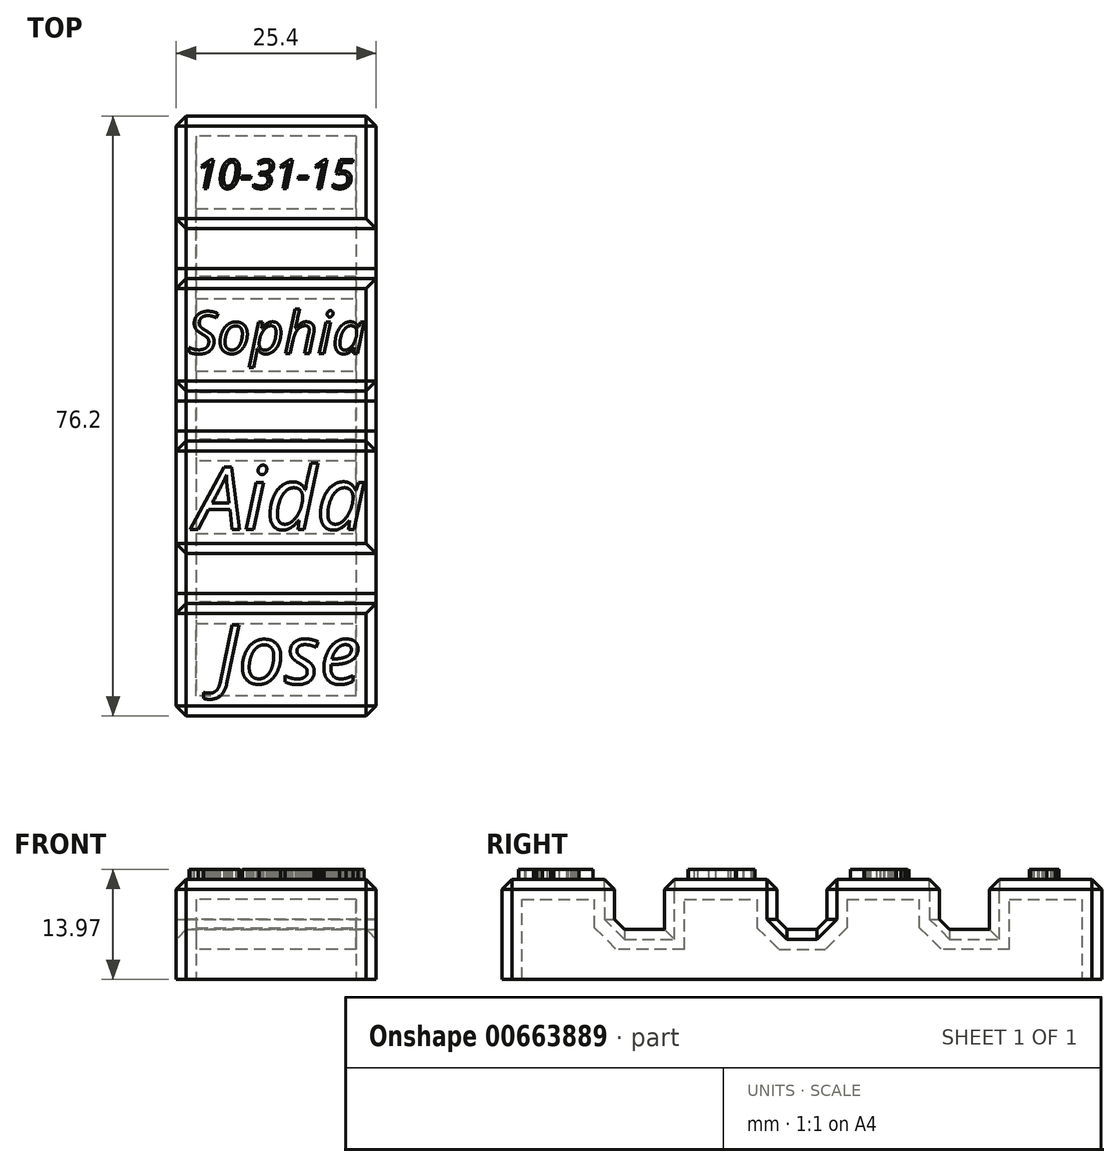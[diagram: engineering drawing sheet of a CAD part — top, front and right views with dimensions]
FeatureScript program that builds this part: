
annotation { "Feature Type Name" : "Feature", "Feature Type Description" : "" }
export const myFeature = defineFeature(function(context is Context, id is Id, definition is map)
    precondition{}
    {
        {
            var Q0;
            Q0=qCreatedBy(makeId("Top.planeOp"),FACE);
            var sketch = newSketch(context, id + "F0", { "sketchPlane" : qUnion([Q0])});
            skLineSegment(sketch, "E0.bottom", {"start": v(12.7, 38.1) * mm, "end": v(-12.7, 38.1) * mm});
            skLineSegment(sketch, "E0.top", {"start": v(12.7, -38.1) * mm, "end": v(-12.7, -38.1) * mm});
            skLineSegment(sketch, "E0.left", {"start": v(12.7, 38.1) * mm, "end": v(12.7, -38.1) * mm});
            skLineSegment(sketch, "E0.right", {"start": v(-12.7, 38.1) * mm, "end": v(-12.7, -38.1) * mm});
            skPoint(sketch, "E0.middle", {"position": v(0, 0) * mm});
            skSolve(sketch);
        }
        {
            var Q0;
            Q0 = qSketchRegion(id + "F0", true);
            extrude(context, id + "F1", {"entities" : qUnion([Q0]), "depth" : 12.7 * mm, "offsetDistance" : 25.4 * mm});
        }
        {
            var Q0;
            Q0=makeQuery(id+"F1.opExtrude","SWEPT_FACE",FACE,{"disambiguationData":[OSD([sQuery(id+"F0.wireOp",EDGE,"E0.left")])]});
            var sketch = newSketch(context, id + "F2", { "sketchPlane" : qUnion([Q0])});
            skLineSegment(sketch, "E1", {"start": v(-38.1, 6.35) * mm, "end": v(38.1, 6.35) * mm, "construction": true});
            skLineSegment(sketch, "E2.bottom", {"start": v(3.17, 6.35) * mm, "end": v(-3.18, 6.35) * mm});
            skLineSegment(sketch, "E2.top", {"start": v(3.17, 19.05) * mm, "end": v(-3.18, 19.05) * mm});
            skLineSegment(sketch, "E2.left", {"start": v(3.17, 6.35) * mm, "end": v(3.17, 19.05) * mm});
            skLineSegment(sketch, "E2.right", {"start": v(-3.18, 6.35) * mm, "end": v(-3.18, 19.05) * mm});
            skPoint(sketch, "E2.middle", {"position": v(0, 12.7) * mm});
            skLineSegment(sketch, "E3.bottom", {"start": v(23.83, 6.35) * mm, "end": v(17.48, 6.35) * mm});
            skLineSegment(sketch, "E3.top", {"start": v(23.83, 19.05) * mm, "end": v(17.48, 19.05) * mm});
            skLineSegment(sketch, "E3.left", {"start": v(23.83, 6.35) * mm, "end": v(23.83, 19.05) * mm});
            skLineSegment(sketch, "E3.right", {"start": v(17.48, 6.35) * mm, "end": v(17.48, 19.05) * mm});
            skPoint(sketch, "E3.middle", {"position": v(20.65, 12.7) * mm});
            skLineSegment(sketch, "E4.bottom", {"start": v(-17.48, 6.35) * mm, "end": v(-23.83, 6.35) * mm});
            skLineSegment(sketch, "E4.top", {"start": v(-17.48, 19.05) * mm, "end": v(-23.83, 19.05) * mm});
            skLineSegment(sketch, "E4.left", {"start": v(-17.48, 6.35) * mm, "end": v(-17.48, 19.05) * mm});
            skLineSegment(sketch, "E4.right", {"start": v(-23.83, 6.35) * mm, "end": v(-23.83, 19.05) * mm});
            skPoint(sketch, "E4.middle", {"position": v(-20.65, 12.7) * mm});
            skSolve(sketch);
        }
        {
            var Q0;
            Q0 = qSketchRegion(id + "F2", true);
            extrude(context, id + "F3", {"entities" : qUnion([Q0]), "operationType" : NewBodyOperationType.REMOVE, "endBound" : BoundingType.THROUGH_ALL, "oppositeDirection" : true, "depth" : 25.4 * mm, "offsetDistance" : 25.4 * mm});
        }
        {
            var Q0;
            {var subQ0=sQuery(id+"F0.wireOp",EDGE,"E0.bottom");var subQ1=sQuery(id+"F0.wireOp",EDGE,"E0.right");var subQ2=sQuery(id+"F0.wireOp",EDGE,"E0.left");Q0=makeQuery(id+"F3.boolean.opBoolean","SPLIT",FACE,{"disambiguationData":[TD([makeQuery(id+"F1.opExtrude","SWEPT_FACE",FACE,{"disambiguationData":[OSD([subQ0])]})])],"derivedFrom":makeQuery(id+"F1.opExtrude","CAP_FACE",FACE,{"disambiguationData":[OSD([subQ0,sQuery(id+"F0.wireOp",EDGE,"E0.top"),subQ2,subQ1])],"isStart":false})});}
            var Q1;
            Q1=makeQuery(id+"F3.boolean.opBoolean","COPY",EDGE,{"derivedFrom":makeQuery(id+"F3.opExtrude","CAP_EDGE",EDGE,{"disambiguationData":[OSD([sQuery(id+"F2.wireOp",EDGE,"E4.bottom")])],"isStart":true})});
            var Q2;
            Q2=makeQuery(id+"F3.boolean.opBoolean","COPY",FACE,{"derivedFrom":makeQuery(id+"F3.opExtrude","SWEPT_FACE",FACE,{"disambiguationData":[OSD([sQuery(id+"F2.wireOp",EDGE,"E2.bottom")])]})});
            var Q3;
            Q3=makeQuery(id+"F3.boolean.opBoolean","COPY",EDGE,{"derivedFrom":makeQuery(id+"F3.opExtrude","CAP_EDGE",EDGE,{"disambiguationData":[OSD([sQuery(id+"F2.wireOp",EDGE,"E3.right")])],"isStart":true})});
            var Q4;
            Q4=makeQuery(id+"F3.boolean.opBoolean","COPY",EDGE,{"derivedFrom":makeQuery(id+"F3.opExtrude","CAP_EDGE",EDGE,{"disambiguationData":[OSD([sQuery(id+"F2.wireOp",EDGE,"E3.left")])],"isStart":true})});
            var Q5;
            Q5=makeQuery(id+"F3.boolean.opBoolean","COPY",EDGE,{"derivedFrom":makeQuery(id+"F3.opExtrude","CAP_EDGE",EDGE,{"disambiguationData":[OSD([sQuery(id+"F2.wireOp",EDGE,"E4.right")])],"isStart":true})});
            var Q6;
            Q6=makeQuery(id+"F3.boolean.opBoolean","COPY",EDGE,{"derivedFrom":makeQuery(id+"F3.opExtrude","CAP_EDGE",EDGE,{"disambiguationData":[OSD([sQuery(id+"F2.wireOp",EDGE,"E4.left")])],"isStart":true})});
            var Q7;
            {var subQ0=sQuery(id+"F0.wireOp",EDGE,"E0.top");var subQ1=sQuery(id+"F0.wireOp",EDGE,"E0.left");var subQ2=sQuery(id+"F0.wireOp",EDGE,"E0.right");Q7=makeQuery(id+"F3.boolean.opBoolean","SPLIT",FACE,{"disambiguationData":[TD([makeQuery(id+"F1.opExtrude","SWEPT_FACE",FACE,{"disambiguationData":[OSD([subQ0])]})])],"derivedFrom":makeQuery(id+"F1.opExtrude","CAP_FACE",FACE,{"disambiguationData":[OSD([sQuery(id+"F0.wireOp",EDGE,"E0.bottom"),subQ0,subQ1,subQ2])],"isStart":false})});}
            var Q8;
            Q8=makeQuery(id+"F3.boolean.opBoolean","COPY",EDGE,{"derivedFrom":makeQuery(id+"F3.opExtrude","SWEPT_EDGE",EDGE,{"disambiguationData":[OSD([sQuery(id+"F2.wireOp",EDGE,"E4.bottom"),sQuery(id+"F2.wireOp",EDGE,"E4.right")])]})});
            var Q9;
            {var subQ0=sQuery(id+"F0.wireOp",EDGE,"E0.left");var subQ1=sQuery(id+"F0.wireOp",EDGE,"E0.right");Q9=makeQuery(id+"F3.boolean.opBoolean","SPLIT",FACE,{"disambiguationData":[TD([makeQuery(id+"F3.opExtrude","SWEPT_FACE",FACE,{"disambiguationData":[OSD([sQuery(id+"F2.wireOp",EDGE,"E2.right")])]})])],"derivedFrom":makeQuery(id+"F1.opExtrude","CAP_FACE",FACE,{"disambiguationData":[OSD([sQuery(id+"F0.wireOp",EDGE,"E0.bottom"),sQuery(id+"F0.wireOp",EDGE,"E0.top"),subQ0,subQ1])],"isStart":false})});}
            var Q10;
            {var subQ0=sQuery(id+"F0.wireOp",EDGE,"E0.left");var subQ1=sQuery(id+"F0.wireOp",EDGE,"E0.right");Q10=makeQuery(id+"F3.boolean.opBoolean","SPLIT",FACE,{"disambiguationData":[TD([makeQuery(id+"F3.opExtrude","SWEPT_FACE",FACE,{"disambiguationData":[OSD([sQuery(id+"F2.wireOp",EDGE,"E2.left")])]})])],"derivedFrom":makeQuery(id+"F1.opExtrude","CAP_FACE",FACE,{"disambiguationData":[OSD([sQuery(id+"F0.wireOp",EDGE,"E0.bottom"),sQuery(id+"F0.wireOp",EDGE,"E0.top"),subQ0,subQ1])],"isStart":false})});}
            var Q11;
            Q11=makeQuery(id+"F3.boolean.opBoolean","COPY",EDGE,{"derivedFrom":makeQuery(id+"F3.opExtrude","SWEPT_EDGE",EDGE,{"disambiguationData":[OSD([sQuery(id+"F2.wireOp",EDGE,"E3.bottom"),sQuery(id+"F2.wireOp",EDGE,"E3.right")])]})});
            var Q12;
            Q12=makeQuery(id+"F3.boolean.opBoolean","INTERSECT",EDGE,{"derivedFrom":[makeQuery(id+"F1.opExtrude","SWEPT_FACE",FACE,{"disambiguationData":[OSD([sQuery(id+"F0.wireOp",EDGE,"E0.right")])]}),makeQuery(id+"F3.opExtrude","SWEPT_FACE",FACE,{"disambiguationData":[OSD([sQuery(id+"F2.wireOp",EDGE,"E3.bottom")])]})]});
            var Q13;
            Q13=makeQuery(id+"F3.boolean.opBoolean","INTERSECT",EDGE,{"derivedFrom":[makeQuery(id+"F1.opExtrude","SWEPT_FACE",FACE,{"disambiguationData":[OSD([sQuery(id+"F0.wireOp",EDGE,"E0.right")])]}),makeQuery(id+"F3.opExtrude","SWEPT_FACE",FACE,{"disambiguationData":[OSD([sQuery(id+"F2.wireOp",EDGE,"E3.left")])]})]});
            var Q14;
            Q14=makeQuery(id+"F3.boolean.opBoolean","INTERSECT",EDGE,{"derivedFrom":[makeQuery(id+"F1.opExtrude","SWEPT_FACE",FACE,{"disambiguationData":[OSD([sQuery(id+"F0.wireOp",EDGE,"E0.right")])]}),makeQuery(id+"F3.opExtrude","SWEPT_FACE",FACE,{"disambiguationData":[OSD([sQuery(id+"F2.wireOp",EDGE,"E4.right")])]})]});
            var Q15;
            Q15=makeQuery(id+"F3.boolean.opBoolean","INTERSECT",EDGE,{"derivedFrom":[makeQuery(id+"F1.opExtrude","SWEPT_FACE",FACE,{"disambiguationData":[OSD([sQuery(id+"F0.wireOp",EDGE,"E0.right")])]}),makeQuery(id+"F3.opExtrude","SWEPT_FACE",FACE,{"disambiguationData":[OSD([sQuery(id+"F2.wireOp",EDGE,"E4.left")])]})]});
            var Q16;
            Q16=makeQuery(id+"F1.opExtrude","SWEPT_EDGE",EDGE,{"disambiguationData":[OSD([sQuery(id+"F0.wireOp",EDGE,"E0.bottom"),sQuery(id+"F0.wireOp",EDGE,"E0.right")])]});
            var Q17;
            Q17=makeQuery(id+"F1.opExtrude","SWEPT_EDGE",EDGE,{"disambiguationData":[OSD([sQuery(id+"F0.wireOp",EDGE,"E0.top"),sQuery(id+"F0.wireOp",EDGE,"E0.right")])]});
            var Q18;
            Q18=makeQuery(id+"F1.opExtrude","SWEPT_EDGE",EDGE,{"disambiguationData":[OSD([sQuery(id+"F0.wireOp",EDGE,"E0.top"),sQuery(id+"F0.wireOp",EDGE,"E0.left")])]});
            var Q19;
            Q19=makeQuery(id+"F1.opExtrude","SWEPT_EDGE",EDGE,{"disambiguationData":[OSD([sQuery(id+"F0.wireOp",EDGE,"E0.bottom"),sQuery(id+"F0.wireOp",EDGE,"E0.left")])]});
            var Q20;
            Q20=makeQuery(id+"F3.boolean.opBoolean","INTERSECT",EDGE,{"derivedFrom":[makeQuery(id+"F1.opExtrude","SWEPT_FACE",FACE,{"disambiguationData":[OSD([sQuery(id+"F0.wireOp",EDGE,"E0.right")])]}),makeQuery(id+"F3.opExtrude","SWEPT_FACE",FACE,{"disambiguationData":[OSD([sQuery(id+"F2.wireOp",EDGE,"E4.bottom")])]})]});
            chamfer(context, id + "F4", {"entities" : qUnion([Q0, Q1, Q2, Q3, Q4, Q5, Q6, Q7, Q8, Q9, Q10, Q11, Q12, Q13, Q14, Q15, Q16, Q17, Q18, Q19, Q20]), "width" : 1.27 * mm, "tangentPropagation" : true});
        }
        {
            var Q0;
            Q0=makeQuery(id+"F1.opExtrude","CAP_FACE",FACE,{"disambiguationData":[OSD([sQuery(id+"F0.wireOp",EDGE,"E0.bottom"),sQuery(id+"F0.wireOp",EDGE,"E0.top"),sQuery(id+"F0.wireOp",EDGE,"E0.left"),sQuery(id+"F0.wireOp",EDGE,"E0.right")])],"isStart":true});
            shell(context, id + "F5", {"entities" : qUnion([Q0]), "thickness" : 2.54 * mm});
        }
        {
            var Q0;
            {var subQ0=sQuery(id+"F0.wireOp",EDGE,"E0.top");var subQ1=sQuery(id+"F0.wireOp",EDGE,"E0.left");var subQ2=sQuery(id+"F0.wireOp",EDGE,"E0.right");Q0=makeQuery(id+"F3.boolean.opBoolean","SPLIT",FACE,{"disambiguationData":[TD([makeQuery(id+"F1.opExtrude","SWEPT_FACE",FACE,{"disambiguationData":[OSD([subQ0])]})])],"derivedFrom":makeQuery(id+"F1.opExtrude","CAP_FACE",FACE,{"disambiguationData":[OSD([sQuery(id+"F0.wireOp",EDGE,"E0.bottom"),subQ0,subQ1,subQ2])],"isStart":false})});}
            var sketch = newSketch(context, id + "F6", { "sketchPlane" : qUnion([Q0])});
            skText(sketch, "E5", { "text": "Jose", "fontName": "OpenSans-Italic.ttf"});
            const initialGuessF6  = {"E5": [-0.0076, -0.03402, 1, 0, 0.00754]};
            skSetInitialGuess(sketch, initialGuessF6);
            skSolve(sketch);
        }
        {
            var Q0;
            Q0 = qSketchRegion(id + "F6", true);
            extrude(context, id + "F7", {"entities" : qUnion([Q0]), "operationType" : NewBodyOperationType.ADD, "depth" : 1.27 * mm, "offsetDistance" : 25.4 * mm});
        }
        {
            var Q0;
            {var subQ0=sQuery(id+"F0.wireOp",EDGE,"E0.left");var subQ1=sQuery(id+"F0.wireOp",EDGE,"E0.right");Q0=makeQuery(id+"F3.boolean.opBoolean","SPLIT",FACE,{"disambiguationData":[TD([makeQuery(id+"F3.opExtrude","SWEPT_FACE",FACE,{"disambiguationData":[OSD([sQuery(id+"F2.wireOp",EDGE,"E2.right")])]})])],"derivedFrom":makeQuery(id+"F1.opExtrude","CAP_FACE",FACE,{"disambiguationData":[OSD([sQuery(id+"F0.wireOp",EDGE,"E0.bottom"),sQuery(id+"F0.wireOp",EDGE,"E0.top"),subQ0,subQ1])],"isStart":false})});}
            var sketch = newSketch(context, id + "F8", { "sketchPlane" : qUnion([Q0])});
            skText(sketch, "E6", { "text": "Aida", "fontName": "OpenSans-Italic.ttf"});
            const initialGuessF8  = {"E6": [-0.0103, -0.0144, 1, 0, 0.008]};
            skSetInitialGuess(sketch, initialGuessF8);
            skSolve(sketch);
        }
        {
            var Q0;
            Q0 = qSketchRegion(id + "F8", true);
            extrude(context, id + "F9", {"entities" : qUnion([Q0]), "operationType" : NewBodyOperationType.ADD, "depth" : 1.27 * mm, "offsetDistance" : 25.4 * mm});
        }
        {
            var Q0;
            {var subQ0=sQuery(id+"F0.wireOp",EDGE,"E0.left");var subQ1=sQuery(id+"F0.wireOp",EDGE,"E0.right");Q0=makeQuery(id+"F3.boolean.opBoolean","SPLIT",FACE,{"disambiguationData":[TD([makeQuery(id+"F3.opExtrude","SWEPT_FACE",FACE,{"disambiguationData":[OSD([sQuery(id+"F2.wireOp",EDGE,"E2.left")])]})])],"derivedFrom":makeQuery(id+"F1.opExtrude","CAP_FACE",FACE,{"disambiguationData":[OSD([sQuery(id+"F0.wireOp",EDGE,"E0.bottom"),sQuery(id+"F0.wireOp",EDGE,"E0.top"),subQ0,subQ1])],"isStart":false})});}
            var sketch = newSketch(context, id + "F10", { "sketchPlane" : qUnion([Q0])});
            skText(sketch, "E7", { "text": "Sophia", "fontName": "OpenSans-Italic.ttf"});
            const initialGuessF10  = {"E7": [-0.0112, 0.00794, 1, 0, 0.00534]};
            skSetInitialGuess(sketch, initialGuessF10);
            skSolve(sketch);
        }
        {
            var Q0;
            Q0 = qSketchRegion(id + "F10", true);
            extrude(context, id + "F11", {"entities" : qUnion([Q0]), "operationType" : NewBodyOperationType.ADD, "depth" : 1.27 * mm, "offsetDistance" : 25.4 * mm});
        }
        {
            var Q0;
            {var subQ0=sQuery(id+"F0.wireOp",EDGE,"E0.bottom");var subQ1=sQuery(id+"F0.wireOp",EDGE,"E0.right");var subQ2=sQuery(id+"F0.wireOp",EDGE,"E0.left");Q0=makeQuery(id+"F3.boolean.opBoolean","SPLIT",FACE,{"disambiguationData":[TD([makeQuery(id+"F1.opExtrude","SWEPT_FACE",FACE,{"disambiguationData":[OSD([subQ0])]})])],"derivedFrom":makeQuery(id+"F1.opExtrude","CAP_FACE",FACE,{"disambiguationData":[OSD([subQ0,sQuery(id+"F0.wireOp",EDGE,"E0.top"),subQ2,subQ1])],"isStart":false})});}
            var sketch = newSketch(context, id + "F12", { "sketchPlane" : qUnion([Q0])});
            skText(sketch, "E8", { "text": "10-31-15", "fontName": "OpenSans-Italic.ttf"});
            const initialGuessF12  = {"E8": [-0.01022, 0.0289, 1, 0, 0.00368]};
            skSetInitialGuess(sketch, initialGuessF12);
            skSolve(sketch);
        }
        {
            var Q0;
            Q0 = qSketchRegion(id + "F12", true);
            extrude(context, id + "F13", {"entities" : qUnion([Q0]), "operationType" : NewBodyOperationType.ADD, "depth" : 1.27 * mm, "offsetDistance" : 25.4 * mm});
        }
    });
